# Revit family: T200182
name_source: partatom
category: Furniture
revit_build: Autodesk Revit Architecture 2015 (Build: 20140322_1515(x64)
units: mm (PartAtom-declared; Revit-internal decimal feet)

## types (1)
- T200182
    Assembly Code = E2020400
    Catalog = https://ofs.com
    Description = OFS TYPICAL T200182
    Manufacturer = OFS
    Model = T200182
    Staks  Benching Rectangular Worksurface = STAKS SURFACE EDGE
    Staks Center Electric Column Leg Caps = OFS STAKS Metal Base Material
    Staks Center Electric Leg Caps = OFS STAKS Leg Caps Material
    Staks Corner Shelf 3D Laminate = OFS STAKS Laminate Material
    Staks Corner Shelf Edge = OFS STAKS Edge Material
    Staks Corner Shelf Veneer = OFS STAKS Surface Material
    Staks Fabric Tackboard = STAKS FABRIC TACKBOARD
    Staks Rectangular Worksurface = STAKS SURFACE EDGE
    Staks Worksurface Height Chasis = OFS STAKS Chasis Wood Grain Laminate
    Staks Worksurface Height Drawer = OFS STAKS Drawer Front Material
    Staks Worksurface Height Drawer Handle = OFS STAKS Handle Material
    URL = https://ofs.com
    Wire Manager Material = OFS STAKS PET Wire Manager Material
    staks Spine or Divider Wall = STAKS SURFACE LG

## geometry (parser evidence)
native form markers: Blend x84, Sweep x24
no freeform markers — native parametric forms only
